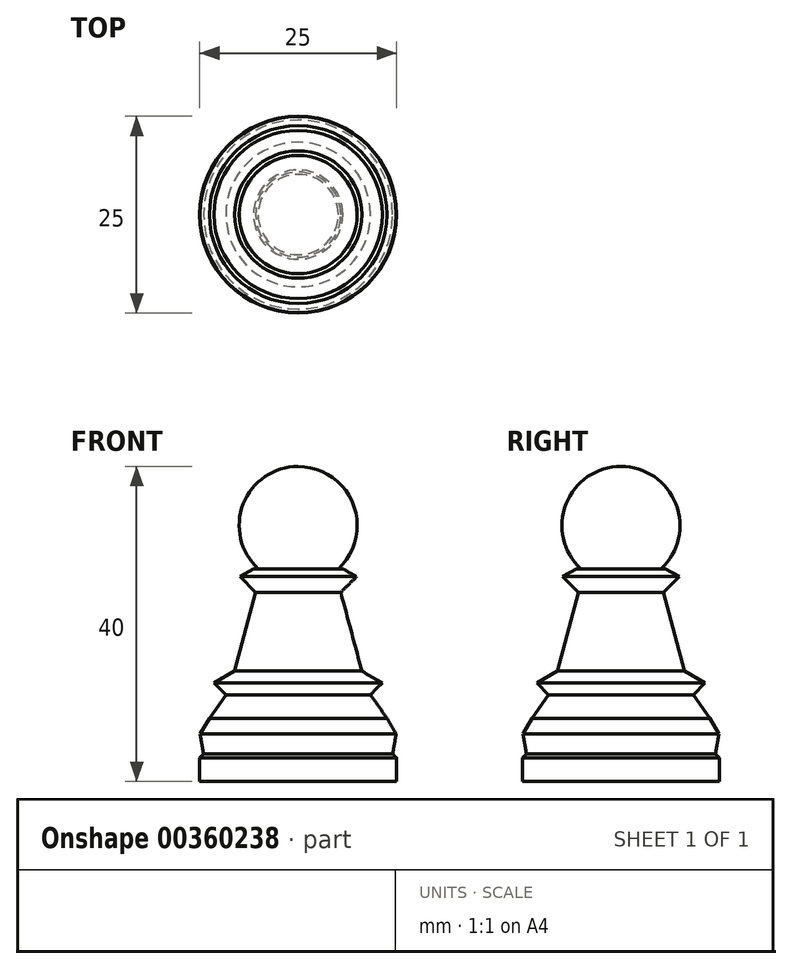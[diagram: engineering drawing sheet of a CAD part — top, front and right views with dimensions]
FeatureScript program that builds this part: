
annotation { "Feature Type Name" : "Feature", "Feature Type Description" : "" }
export const myFeature = defineFeature(function(context is Context, id is Id, definition is map)
    precondition{}
    {
        {
            var Q0;
            Q0=qCreatedBy(makeId("Top.planeOp"),FACE);
            var sketch = newSketch(context, id + "F0", { "sketchPlane" : qUnion([Q0])});
            skCircle(sketch, "E0", {"center": v(0, 0) * mm, "radius": 12.5 * mm});
            skSolve(sketch);
        }
        {
            var Q0;
            Q0=makeQuery(id+"F0.imprint","IMPRINT",FACE,{"disambiguationData":[TD([[makeQuery(id+"F0.imprint","IMPRINT",EDGE,{"derivedFrom":sQuery(id+"F0.wireOp",EDGE,"E0")}),1.0]])]});
            extrude(context, id + "F1", {"entities" : qUnion([Q0]), "depth" : 3 * mm});
        }
        {
            var Q0;
            Q0=makeQuery(id+"F1.opExtrude","CAP_FACE",FACE,{"disambiguationData":[OSD([sQuery(id+"F0.wireOp",EDGE,"E0")])],"isStart":false});
            extrude(context, id + "F2", {"entities" : qUnion([Q0]), "operationType" : NewBodyOperationType.ADD, "depth" : .5 * mm, "hasDraft" : true, "draftAngle" : 45 * degree, "draftPullDirection" : true});
        }
        {
            var Q0;
            Q0=makeQuery(id+"F2.opExtrude","CAP_FACE",FACE,{"disambiguationData":[OSD([sQuery(id+"F0.wireOp",EDGE,"E0")])],"isStart":false});
            extrude(context, id + "F3", {"entities" : qUnion([Q0]), "operationType" : NewBodyOperationType.ADD, "depth" : 2.5 * mm, "hasDraft" : true, "draftAngle" : 10 * degree});
        }
        {
            var Q0;
            Q0=makeQuery(id+"F3.opExtrude","CAP_FACE",FACE,{"disambiguationData":[OSD([sQuery(id+"F0.wireOp",EDGE,"E0")])],"isStart":false});
            extrude(context, id + "F4", {"entities" : qUnion([Q0]), "operationType" : NewBodyOperationType.ADD, "depth" : 2 * mm, "hasDraft" : true, "draftAngle" : 30 * degree, "draftPullDirection" : true});
        }
        {
            var Q0;
            Q0=makeQuery(id+"F4.opExtrude","CAP_FACE",FACE,{"disambiguationData":[OSD([sQuery(id+"F0.wireOp",EDGE,"E0")])],"isStart":false});
            extrude(context, id + "F5", {"entities" : qUnion([Q0]), "operationType" : NewBodyOperationType.ADD, "depth" : 3 * mm, "hasDraft" : true, "draftAngle" : 35 * degree, "draftPullDirection" : true});
        }
        {
            var Q0;
            Q0=makeQuery(id+"F5.opExtrude","CAP_FACE",FACE,{"disambiguationData":[OSD([sQuery(id+"F0.wireOp",EDGE,"E0")])],"isStart":false});
            extrude(context, id + "F6", {"entities" : qUnion([Q0]), "operationType" : NewBodyOperationType.ADD, "depth" : 1.5 * mm, "hasDraft" : true, "draftAngle" : 45 * degree});
        }
        {
            var Q0;
            Q0=makeQuery(id+"F6.opExtrude","CAP_FACE",FACE,{"disambiguationData":[OSD([sQuery(id+"F0.wireOp",EDGE,"E0")])],"isStart":false});
            extrude(context, id + "F7", {"entities" : qUnion([Q0]), "operationType" : NewBodyOperationType.ADD, "depth" : 1.5 * mm, "hasDraft" : true, "draftAngle" : 60 * degree, "draftPullDirection" : true});
        }
        {
            var Q0;
            Q0=makeQuery(id+"F7.opExtrude","CAP_FACE",FACE,{"disambiguationData":[OSD([sQuery(id+"F0.wireOp",EDGE,"E0")])],"isStart":false});
            extrude(context, id + "F8", {"entities" : qUnion([Q0]), "operationType" : NewBodyOperationType.ADD, "depth" : 10 * mm, "hasDraft" : true, "draftAngle" : 15 * degree, "draftPullDirection" : true});
        }
        {
            var Q0;
            Q0=makeQuery(id+"F8.opExtrude","CAP_FACE",FACE,{"disambiguationData":[OSD([sQuery(id+"F0.wireOp",EDGE,"E0")])],"isStart":false});
            extrude(context, id + "F9", {"entities" : qUnion([Q0]), "operationType" : NewBodyOperationType.ADD, "depth" : 2 * mm, "hasDraft" : true, "draftAngle" : 45 * degree});
        }
        {
            var Q0;
            Q0=makeQuery(id+"F9.opExtrude","CAP_FACE",FACE,{"disambiguationData":[OSD([sQuery(id+"F0.wireOp",EDGE,"E0")])],"isStart":false});
            extrude(context, id + "F10", {"entities" : qUnion([Q0]), "operationType" : NewBodyOperationType.ADD, "depth" : 1 * mm, "hasDraft" : true, "draftAngle" : 60 * degree, "draftPullDirection" : true});
        }
        {
            var Q0;
            Q0=qCreatedBy(makeId("Front.planeOp"),FACE);
            var sketch = newSketch(context, id + "F11", { "sketchPlane" : qUnion([Q0])});
            skCircle(sketch, "E1", {"center": v(0, 32.5) * mm, "radius": 7.5 * mm});
            skLineSegment(sketch, "E2", {"start": v(0, 0) * mm, "end": v(0, 52.42) * mm});
            skSolve(sketch);
        }
        {
            var Q0;
            {var subQ0=sQuery(id+"F11.wireOp",EDGE,"E2");var subQ1=sQuery(id+"F11.wireOp",EDGE,"E1");var subQ2=makeQuery(id+"F11.imprint","INTERSECT",VERTEX,{"disambiguationData":[OD(0.0)],"derivedFrom":[subQ1,subQ0]});Q0=makeQuery(id+"F11.imprint","IMPRINT",FACE,{"disambiguationData":[TD([[makeQuery(id+"F11.imprint","IMPRINT",EDGE,{"disambiguationData":[TD([[subQ2,1.0]])],"derivedFrom":subQ1}),1.0]])]});}
            var Q1;
            Q1=sQuery(id+"F11.wireOp",EDGE,"E2");
            revolve(context, id + "F12", {"operationType" : NewBodyOperationType.ADD, "entities" : qUnion([Q0]), "axis" : qUnion([Q1]), "revolveType" : RevolveType.FULL});
        }
    });
